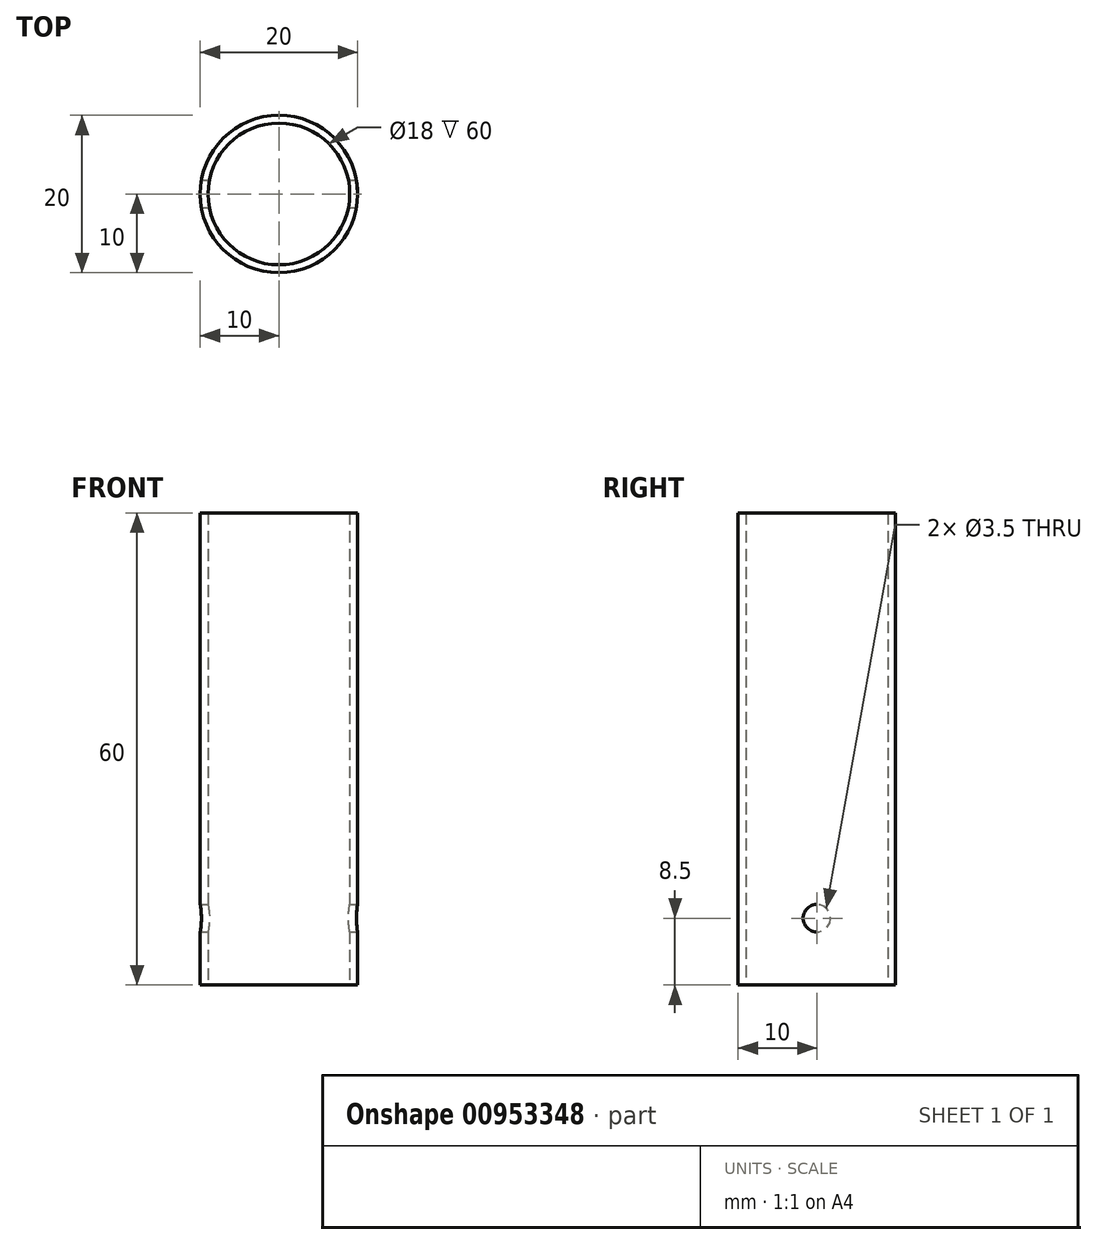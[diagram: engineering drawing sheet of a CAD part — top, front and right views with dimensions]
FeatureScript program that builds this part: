
annotation { "Feature Type Name" : "Feature", "Feature Type Description" : "" }
export const myFeature = defineFeature(function(context is Context, id is Id, definition is map)
    precondition{}
    {
        {
            var Q0;
            Q0=qCreatedBy(makeId("Top.planeOp"),FACE);
            var sketch = newSketch(context, id + "F0", { "sketchPlane" : qUnion([Q0])});
            skCircle(sketch, "E0", {"center": v(0, 0) * mm, "radius": 10 * mm});
            skCircle(sketch, "E1.0", {"center": v(0, 0) * mm, "radius": 9 * mm});
            skSolve(sketch);
        }
        {
            var Q0;
            Q0=makeQuery(id+"F0.imprint","IMPRINT",FACE,{"disambiguationData":[TD([[makeQuery(id+"F0.imprint","IMPRINT",EDGE,{"derivedFrom":sQuery(id+"F0.wireOp",EDGE,"E0")}),1.0]])]});
            extrude(context, id + "F1", {"entities" : qUnion([Q0]), "endBound" : BoundingType.SYMMETRIC, "depth" : 60 * mm, "offsetDistance" : 25 * mm});
        }
        {
            var Q0;
            Q0=qCreatedBy(makeId("Right.planeOp"),FACE);
            var sketch = newSketch(context, id + "F2", { "sketchPlane" : qUnion([Q0])});
            skCircle(sketch, "E2", {"center": v(0, -21.5) * mm, "radius": 1.75 * mm});
            skSolve(sketch);
        }
        {
            var Q0;
            Q0=qSketchRegion(id+"F2",true);
            extrude(context, id + "F3", {"entities" : qUnion([Q0]), "operationType" : NewBodyOperationType.REMOVE, "endBound" : BoundingType.SYMMETRIC, "oppositeDirection" : true, "depth" : 25 * mm, "offsetDistance" : 25 * mm});
        }
    });
